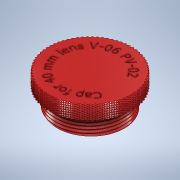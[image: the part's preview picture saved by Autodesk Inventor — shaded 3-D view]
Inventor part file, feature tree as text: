
AUTODESK INVENTOR PART (.ipt)
format: ipt  version: 2021.2 (Build 252289000, 289)  size: 8,450,048 bytes
history: native  units: in
note: dims shown in document units (in); Inventor stores cm internally (conversion verified against a paired STEP export)
features: sketch x3, helix x2, revolve x1, extrude x1, plane x1, pattern_circular x1, mirror x1
ambient origin geometry x8: Origin, YZ Plane, XZ Plane, XY Plane, X Axis, Y Axis, Z Axis, Center Point
bodies: Body1 (feature_tree)
feature tree (10):
  revolve  "Revolution3"  [1 undecoded]
  helix  "Coil6"  [1 undecoded]
  extrude  "Extrusion1"  TaperAngle=90.0deg  [1 undecoded]
  plane  "Work Plane1"
  helix  "Coil7"  [1 undecoded]
  pattern_circular  "Circular Pattern1"  [2 undecoded]
  mirror  "Mirror1"
  sketch  "Sketch7"  dims[d9=0.1875in d71=0.375in d72=0.5in]
  sketch  "Sketch11"  dims[d73=0.928in d74=90.0deg d78=0.125in]
  sketch  "Sketch13"  dims[d100=60.0deg d102=0.0102in d103=0.8739in d104=0.0833in d105=0.6667in d106=0.3937in d107=0.0in d108=90.0deg d109=90.0deg d110=0.0in d111=0.0in d113=0.075in d114=0.0in d117=0.803in d118=1.125in d121=0.3in d122=0.5in d123=60.0deg d124=60.0deg d126=0.0833in d127=0.928in d128=-0.1875in d129=0.0344in d130=0.0312in d131=1.0in d132=0.375in d133=0.0492in d134=0.0in d135=90.0deg d136=90.0deg d137=0.0in d138=0.0in d139=28.3465in d140=360.0deg]
note: 6 required parameter values undecoded (feature->parameter linkage not recoverable at this tier; creation-order binding heuristic only, values carry confidence <= 0.55)